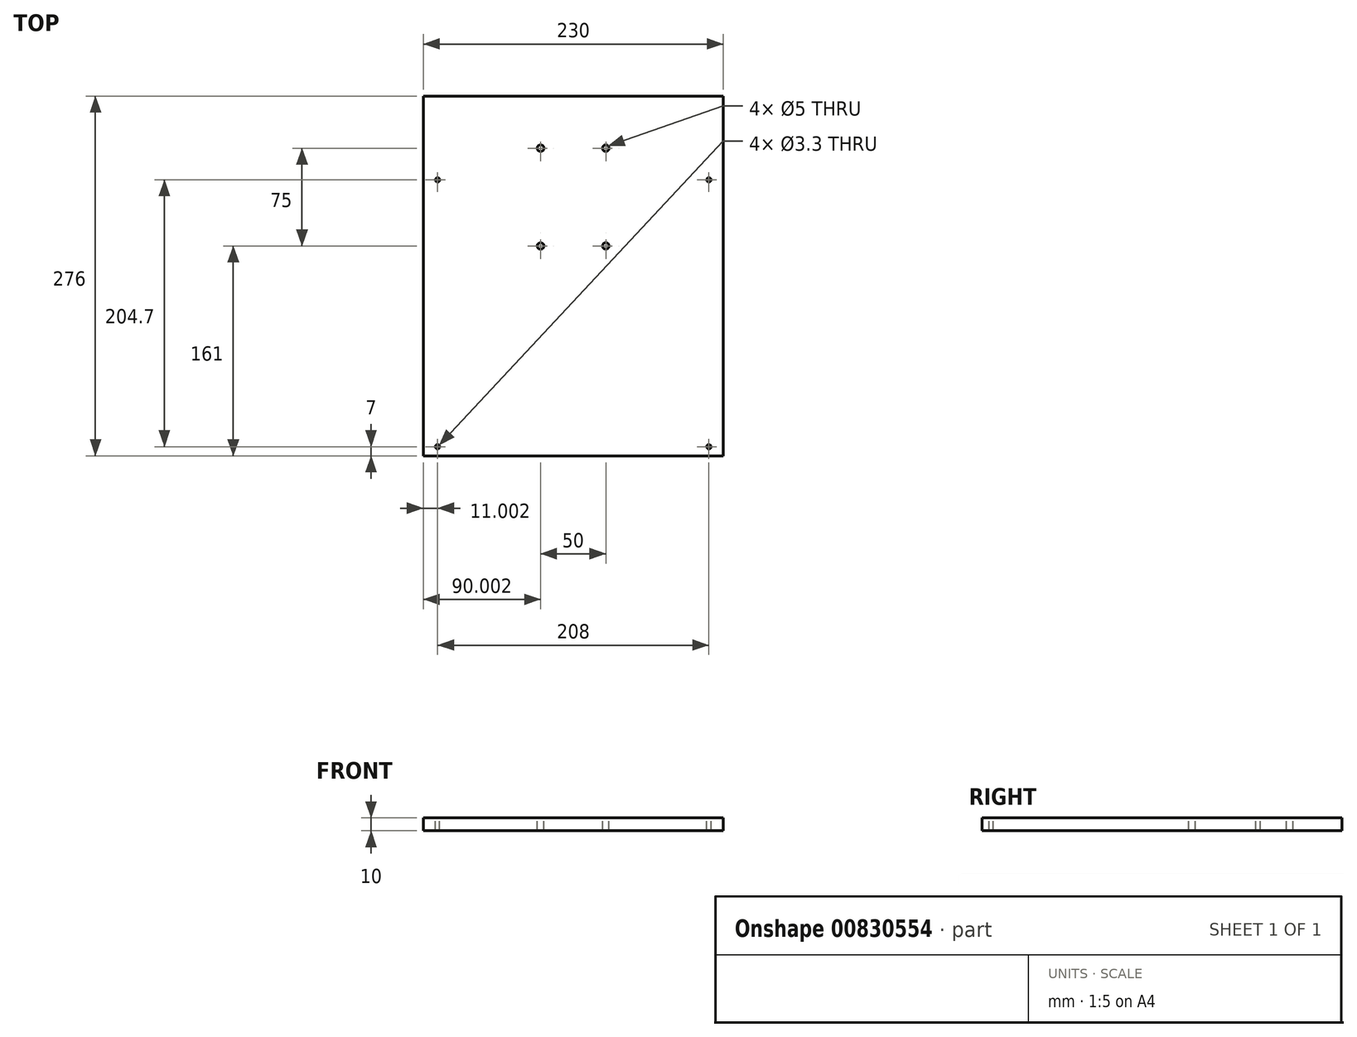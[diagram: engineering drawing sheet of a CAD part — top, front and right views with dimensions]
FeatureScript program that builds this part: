
annotation { "Feature Type Name" : "Feature", "Feature Type Description" : "" }
export const myFeature = defineFeature(function(context is Context, id is Id, definition is map)
    precondition{}
    {
        {
            var Q0;
            Q0=qCreatedBy(makeId("Top.planeOp"),FACE);
            var sketch = newSketch(context, id + "F0", { "sketchPlane" : qUnion([Q0])});
            skLineSegment(sketch, "E0.bottom", {"start": v(-44.88, 134.19) * mm, "end": v(185.12, 134.19) * mm});
            skLineSegment(sketch, "E0.top", {"start": v(-44.88, -141.81) * mm, "end": v(185.12, -141.81) * mm});
            skLineSegment(sketch, "E0.left", {"start": v(-44.88, 134.19) * mm, "end": v(-44.88, -141.81) * mm});
            skLineSegment(sketch, "E0.right", {"start": v(185.12, 134.19) * mm, "end": v(185.12, -141.81) * mm});
            skSolve(sketch);
        }
        {
            var Q0;
            Q0=qSketchRegion(id+"F0",true);
            extrude(context, id + "F1", {"entities" : qUnion([Q0]), "depth" : 10 * mm});
        }
        {
            var Q0;
            Q0=makeQuery(id+"F1.opExtrude","CAP_FACE",FACE,{"disambiguationData":[OSD([sQuery(id+"F0.wireOp",EDGE,"E0.bottom"),sQuery(id+"F0.wireOp",EDGE,"E0.top"),sQuery(id+"F0.wireOp",EDGE,"E0.left"),sQuery(id+"F0.wireOp",EDGE,"E0.right")])],"isStart":false});
            var sketch = newSketch(context, id + "F2", { "sketchPlane" : qUnion([Q0])});
            skLineSegment(sketch, "E1", {"start": v(70.12, 134.19) * mm, "end": v(70.12, -141.81) * mm, "construction": true});
            skLineSegment(sketch, "E2.bottom", {"start": v(45.12, 94.19) * mm, "end": v(95.12, 94.19) * mm, "construction": true});
            skLineSegment(sketch, "E2.top", {"start": v(45.12, 19.19) * mm, "end": v(95.12, 19.19) * mm, "construction": true});
            skLineSegment(sketch, "E2.left", {"start": v(45.12, 94.19) * mm, "end": v(45.12, 19.19) * mm, "construction": true});
            skLineSegment(sketch, "E2.right", {"start": v(95.12, 94.19) * mm, "end": v(95.12, 19.19) * mm, "construction": true});
            skCircle(sketch, "E3", {"center": v(45.12, 94.19) * mm, "radius": 2.5 * mm});
            skCircle(sketch, "E4", {"center": v(95.12, 94.19) * mm, "radius": 2.5 * mm});
            skCircle(sketch, "E5", {"center": v(45.12, 19.19) * mm, "radius": 2.5 * mm});
            skCircle(sketch, "E6", {"center": v(95.12, 19.19) * mm, "radius": 2.5 * mm});
            skLineSegment(sketch, "E7.bottom", {"start": v(-33.88, 69.89) * mm, "end": v(174.12, 69.89) * mm, "construction": true});
            skLineSegment(sketch, "E7.top", {"start": v(-33.88, -134.81) * mm, "end": v(174.12, -134.81) * mm, "construction": true});
            skLineSegment(sketch, "E7.left", {"start": v(-33.88, 69.89) * mm, "end": v(-33.88, -134.81) * mm, "construction": true});
            skLineSegment(sketch, "E7.right", {"start": v(174.12, 69.89) * mm, "end": v(174.12, -134.81) * mm, "construction": true});
            skCircle(sketch, "E8", {"center": v(-33.88, 69.89) * mm, "radius": 1.65 * mm});
            skCircle(sketch, "E9", {"center": v(174.12, 69.89) * mm, "radius": 1.65 * mm});
            skCircle(sketch, "E10", {"center": v(-33.88, -134.81) * mm, "radius": 1.65 * mm});
            skCircle(sketch, "E11", {"center": v(174.12, -134.81) * mm, "radius": 1.65 * mm});
            skSolve(sketch);
        }
        {
            var Q0;
            Q0=qSketchRegion(id+"F2",true);
            extrude(context, id + "F3", {"entities" : qUnion([Q0]), "operationType" : NewBodyOperationType.REMOVE, "endBound" : BoundingType.THROUGH_ALL, "oppositeDirection" : true, "depth" : 25 * mm, "offsetDistance" : 25 * mm});
        }
    });
